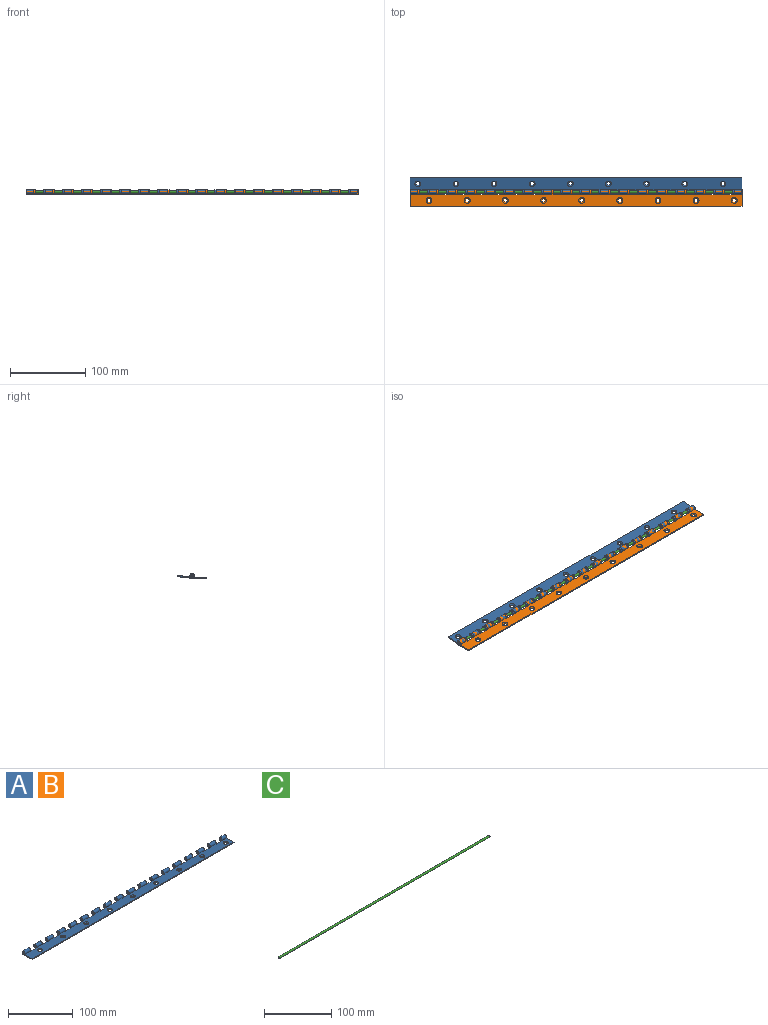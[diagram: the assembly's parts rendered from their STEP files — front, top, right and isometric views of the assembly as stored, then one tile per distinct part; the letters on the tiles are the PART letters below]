
ASSEMBLY  parts=3 mates=2
PART A: 119 faces, bbox 442.2x22.2x6.2 mm
  f0: cylinder r=1.59mm len=12.7mm, axis (-1,0,0), area 105.5mm2, adj f17,f36,f105,f108
  f1: cylinder r=1.59mm len=12.7mm, axis (-1,0,0), area 105.5mm2, adj f17,f37,f102,f106
  f2: cylinder r=1.59mm len=12.7mm, axis (-1,0,0), area 105.5mm2, adj f17,f38,f99,f103
  f3: cylinder r=1.59mm len=12.7mm, axis (-1,0,0), area 105.5mm2, adj f17,f39,f96,f100
  f4: cylinder r=1.59mm len=12.7mm, axis (-1,0,0), area 105.5mm2, adj f17,f40,f93,f97
  f5: cylinder r=1.59mm len=12.7mm, axis (-1,0,0), area 105.5mm2, adj f17,f41,f90,f94
  f6: cylinder r=1.59mm len=12.7mm, axis (-1,0,0), area 105.5mm2, adj f17,f42,f87,f91
  f7: cylinder r=1.59mm len=12.7mm, axis (-1,0,0), area 105.5mm2, adj f17,f43,f84,f88
  f8: cylinder r=1.59mm len=12.7mm, axis (-1,0,0), area 105.5mm2, adj f17,f44,f81,f85
  f9: cylinder r=1.59mm len=12.7mm, axis (-1,0,0), area 105.5mm2, adj f17,f45,f78,f82
  f10: cylinder r=1.59mm len=12.7mm, axis (-1,0,0), area 105.5mm2, adj f17,f46,f75,f79
  f11: cylinder r=1.59mm len=12.7mm, axis (-1,0,0), area 105.5mm2, adj f17,f47,f72,f76
  f12: cylinder r=1.59mm len=12.7mm, axis (-1,0,0), area 105.5mm2, adj f17,f48,f69,f73
  f13: cylinder r=1.59mm len=12.7mm, axis (-1,0,0), area 105.5mm2, adj f17,f49,f66,f70
  f14: cylinder r=1.59mm len=12.7mm, axis (-1,0,0), area 105.5mm2, adj f17,f50,f63,f67
  f15: cylinder r=1.59mm len=12.7mm, axis (-1,0,0), area 105.5mm2, adj f17,f51,f60,f64
  f16: cylinder r=1.59mm len=10.36mm, axis (-1,0,0), area 86mm2, adj f17,f52,f57,f61
  f17: plane 442.16x19.05mm, normal (0,0,1), area 7294.2mm2, adj f0,f1,f2,f3,f4,f5,f6,f7
  f18: plane 442.16x19.05mm, normal (0,0,-1), area 7536.7mm2, adj f19,f20,f21,f22,f23,f24,f25,f26
  f19: cylinder r=3.11mm len=12.7mm, axis (-1,0,0), area 206.7mm2, adj f18,f36,f105,f108
  f20: cylinder r=3.11mm len=12.7mm, axis (-1,0,0), area 206.7mm2, adj f18,f37,f102,f106
  f21: cylinder r=3.11mm len=12.7mm, axis (-1,0,0), area 206.7mm2, adj f18,f38,f99,f103
  f22: cylinder r=3.11mm len=12.7mm, axis (-1,0,0), area 206.7mm2, adj f18,f39,f96,f100
  f23: cylinder r=3.11mm len=12.7mm, axis (-1,0,0), area 206.7mm2, adj f18,f40,f93,f97
  f24: cylinder r=3.11mm len=12.7mm, axis (-1,0,0), area 206.7mm2, adj f18,f41,f90,f94
  f25: cylinder r=3.11mm len=12.7mm, axis (-1,0,0), area 206.7mm2, adj f18,f42,f87,f91
  f26: cylinder r=3.11mm len=12.7mm, axis (-1,0,0), area 206.7mm2, adj f18,f43,f84,f88
  f27: cylinder r=3.11mm len=12.7mm, axis (-1,0,0), area 206.7mm2, adj f18,f44,f81,f85
  f28: cylinder r=3.11mm len=12.7mm, axis (-1,0,0), area 206.7mm2, adj f18,f45,f78,f82
  f29: cylinder r=3.11mm len=12.7mm, axis (-1,0,0), area 206.7mm2, adj f18,f46,f75,f79
  f30: cylinder r=3.11mm len=12.7mm, axis (-1,0,0), area 206.7mm2, adj f18,f47,f72,f76
  f31: cylinder r=3.11mm len=12.7mm, axis (-1,0,0), area 206.7mm2, adj f18,f48,f69,f73
  f32: cylinder r=3.11mm len=12.7mm, axis (-1,0,0), area 206.7mm2, adj f18,f49,f66,f70
  f33: cylinder r=3.11mm len=12.7mm, axis (-1,0,0), area 206.7mm2, adj f18,f50,f63,f67
  f34: cylinder r=3.11mm len=12.7mm, axis (-1,0,0), area 206.7mm2, adj f18,f51,f60,f64
  f35: cylinder r=3.11mm len=10.36mm, axis (-1,0,0), area 168.7mm2, adj f18,f52,f57,f61
  f36: plane 12.7x1.32mm, normal (0,0.5,-0.87), area 19.4mm2, adj f0,f19,f105,f108
  f37: plane 12.7x1.32mm, normal (0,0.5,-0.87), area 19.4mm2, adj f1,f20,f102,f106
  f38: plane 12.7x1.32mm, normal (0,0.5,-0.87), area 19.4mm2, adj f2,f21,f99,f103
  f39: plane 12.7x1.32mm, normal (0,0.5,-0.87), area 19.4mm2, adj f3,f22,f96,f100
  f40: plane 12.7x1.32mm, normal (0,0.5,-0.87), area 19.4mm2, adj f4,f23,f93,f97
  f41: plane 12.7x1.32mm, normal (0,0.5,-0.87), area 19.4mm2, adj f5,f24,f90,f94
  f42: plane 12.7x1.32mm, normal (0,0.5,-0.87), area 19.4mm2, adj f6,f25,f87,f91
  f43: plane 12.7x1.32mm, normal (0,0.5,-0.87), area 19.4mm2, adj f7,f26,f84,f88
  f44: plane 12.7x1.32mm, normal (0,0.5,-0.87), area 19.4mm2, adj f8,f27,f81,f85
  f45: plane 12.7x1.32mm, normal (0,0.5,-0.87), area 19.4mm2, adj f9,f28,f78,f82
  f46: plane 12.7x1.32mm, normal (0,0.5,-0.87), area 19.4mm2, adj f10,f29,f75,f79
  f47: plane 12.7x1.32mm, normal (0,0.5,-0.87), area 19.4mm2, adj f11,f30,f72,f76
  f48: plane 12.7x1.32mm, normal (0,0.5,-0.87), area 19.4mm2, adj f12,f31,f69,f73
  f49: plane 12.7x1.32mm, normal (0,0.5,-0.87), area 19.4mm2, adj f13,f32,f66,f70
  f50: plane 12.7x1.32mm, normal (0,0.5,-0.87), area 19.4mm2, adj f14,f33,f63,f67
  f51: plane 12.7x1.32mm, normal (0,0.5,-0.87), area 19.4mm2, adj f15,f34,f60,f64
  f52: plane 10.36x1.32mm, normal (0,0.5,-0.87), area 15.8mm2, adj f16,f35,f57,f61
  f53: cylinder r=1.59mm len=12.7mm, axis (-1,0,0), area 105.5mm2, adj f17,f56,f58,f109
  f54: plane 442.16x1.52mm, normal (0,-1,0), area 673.9mm2, adj f17,f18,f57,f58
  f55: cylinder r=3.11mm len=12.7mm, axis (-1,0,0), area 206.7mm2, adj f18,f56,f58,f109
  f56: plane 12.7x1.32mm, normal (0,0.5,-0.87), area 19.4mm2, adj f53,f55,f58,f109
  f57: plane 22.16x6.22mm, normal (1,0,0), area 47.8mm2, adj f16,f17,f18,f35,f52,f54
  f58: plane 22.16x6.22mm, normal (-1,0,0), area 47.8mm2, adj f17,f18,f53,f54,f55,f56
  f59: plane 12.7x1.52mm, normal (0,1,0), area 19.4mm2, adj f17,f18,f60,f61
  f60: plane 6.35x6.22mm, normal (1,0,0), area 23.7mm2, adj f15,f17,f18,f34,f51,f59
  f61: plane 6.35x6.22mm, normal (-1,0,0), area 23.7mm2, adj f16,f17,f18,f35,f52,f59
  f62: plane 12.7x1.52mm, normal (0,1,0), area 19.4mm2, adj f17,f18,f63,f64
  f63: plane 6.35x6.22mm, normal (1,0,0), area 23.7mm2, adj f14,f17,f18,f33,f50,f62
  f64: plane 6.35x6.22mm, normal (-1,0,0), area 23.7mm2, adj f15,f17,f18,f34,f51,f62
  f65: plane 12.7x1.52mm, normal (0,1,0), area 19.4mm2, adj f17,f18,f66,f67
  f66: plane 6.35x6.22mm, normal (1,0,0), area 23.7mm2, adj f13,f17,f18,f32,f49,f65
  f67: plane 6.35x6.22mm, normal (-1,0,0), area 23.7mm2, adj f14,f17,f18,f33,f50,f65
  f68: plane 12.7x1.52mm, normal (0,1,0), area 19.4mm2, adj f17,f18,f69,f70
  f69: plane 6.35x6.22mm, normal (1,0,0), area 23.7mm2, adj f12,f17,f18,f31,f48,f68
  f70: plane 6.35x6.22mm, normal (-1,0,0), area 23.7mm2, adj f13,f17,f18,f32,f49,f68
  f71: plane 12.7x1.52mm, normal (0,1,0), area 19.4mm2, adj f17,f18,f72,f73
  f72: plane 6.35x6.22mm, normal (1,0,0), area 23.7mm2, adj f11,f17,f18,f30,f47,f71
  f73: plane 6.35x6.22mm, normal (-1,0,0), area 23.7mm2, adj f12,f17,f18,f31,f48,f71
  f74: plane 12.7x1.52mm, normal (0,1,0), area 19.4mm2, adj f17,f18,f75,f76
  f75: plane 6.35x6.22mm, normal (1,0,0), area 23.7mm2, adj f10,f17,f18,f29,f46,f74
  f76: plane 6.35x6.22mm, normal (-1,0,0), area 23.7mm2, adj f11,f17,f18,f30,f47,f74
  f77: plane 12.7x1.52mm, normal (0,1,0), area 19.4mm2, adj f17,f18,f78,f79
  f78: plane 6.35x6.22mm, normal (1,0,0), area 23.7mm2, adj f9,f17,f18,f28,f45,f77
  f79: plane 6.35x6.22mm, normal (-1,0,0), area 23.7mm2, adj f10,f17,f18,f29,f46,f77
  f80: plane 12.7x1.52mm, normal (0,1,0), area 19.4mm2, adj f17,f18,f81,f82
  f81: plane 6.35x6.22mm, normal (1,0,0), area 23.7mm2, adj f8,f17,f18,f27,f44,f80
  f82: plane 6.35x6.22mm, normal (-1,0,0), area 23.7mm2, adj f9,f17,f18,f28,f45,f80
  f83: plane 12.7x1.52mm, normal (0,1,0), area 19.4mm2, adj f17,f18,f84,f85
  f84: plane 6.35x6.22mm, normal (1,0,0), area 23.7mm2, adj f7,f17,f18,f26,f43,f83
  f85: plane 6.35x6.22mm, normal (-1,0,0), area 23.7mm2, adj f8,f17,f18,f27,f44,f83
  f86: plane 12.7x1.52mm, normal (0,1,0), area 19.4mm2, adj f17,f18,f87,f88
  f87: plane 6.35x6.22mm, normal (1,0,0), area 23.7mm2, adj f6,f17,f18,f25,f42,f86
  f88: plane 6.35x6.22mm, normal (-1,0,0), area 23.7mm2, adj f7,f17,f18,f26,f43,f86
  f89: plane 12.7x1.52mm, normal (0,1,0), area 19.4mm2, adj f17,f18,f90,f91
  f90: plane 6.35x6.22mm, normal (1,0,0), area 23.7mm2, adj f5,f17,f18,f24,f41,f89
  f91: plane 6.35x6.22mm, normal (-1,0,0), area 23.7mm2, adj f6,f17,f18,f25,f42,f89
  f92: plane 12.7x1.52mm, normal (0,1,0), area 19.4mm2, adj f17,f18,f93,f94
  f93: plane 6.35x6.22mm, normal (1,0,0), area 23.7mm2, adj f4,f17,f18,f23,f40,f92
  f94: plane 6.35x6.22mm, normal (-1,0,0), area 23.7mm2, adj f5,f17,f18,f24,f41,f92
  f95: plane 12.7x1.52mm, normal (0,1,0), area 19.4mm2, adj f17,f18,f96,f97
  f96: plane 6.35x6.22mm, normal (1,0,0), area 23.7mm2, adj f3,f17,f18,f22,f39,f95
  f97: plane 6.35x6.22mm, normal (-1,0,0), area 23.7mm2, adj f4,f17,f18,f23,f40,f95
  f98: plane 12.7x1.52mm, normal (0,1,0), area 19.4mm2, adj f17,f18,f99,f100
  f99: plane 6.35x6.22mm, normal (1,0,0), area 23.7mm2, adj f2,f17,f18,f21,f38,f98
  f100: plane 6.35x6.22mm, normal (-1,0,0), area 23.7mm2, adj f3,f17,f18,f22,f39,f98
  f101: plane 12.7x1.52mm, normal (0,1,0), area 19.4mm2, adj f17,f18,f102,f103
  f102: plane 6.35x6.22mm, normal (1,0,0), area 23.7mm2, adj f1,f17,f18,f20,f37,f101
  f103: plane 6.35x6.22mm, normal (-1,0,0), area 23.7mm2, adj f2,f17,f18,f21,f38,f101
  f104: plane 12.7x1.52mm, normal (0,1,0), area 19.4mm2, adj f17,f18,f105,f106
  f105: plane 6.35x6.22mm, normal (1,0,0), area 23.7mm2, adj f0,f17,f18,f19,f36,f104
  f106: plane 6.35x6.22mm, normal (-1,0,0), area 23.7mm2, adj f1,f17,f18,f20,f37,f104
  f107: plane 12.7x1.52mm, normal (0,1,0), area 19.4mm2, adj f17,f18,f108,f109
  f108: plane 6.35x6.22mm, normal (-1,0,0), area 23.7mm2, adj f0,f17,f18,f19,f36,f107
  f109: plane 6.35x6.22mm, normal (1,0,0), area 23.7mm2, adj f17,f18,f53,f55,f56,f107
  f110: cone r=1.83mm half-angle=41deg, axis (0,0,1), area 41.1mm2, adj f17,f18
  f111: cone r=1.83mm half-angle=41deg, axis (0,0,1), area 41.1mm2, adj f17,f18
  f112: cone r=1.83mm half-angle=41deg, axis (0,0,1), area 41.1mm2, adj f17,f18
  f113: cone r=1.83mm half-angle=41deg, axis (0,0,1), area 41.1mm2, adj f17,f18
  f114: cone r=1.83mm half-angle=41deg, axis (0,0,1), area 41.1mm2, adj f17,f18
  f115: cone r=1.83mm half-angle=41deg, axis (0,0,1), area 41.1mm2, adj f17,f18
  f116: cone r=1.83mm half-angle=41deg, axis (0,0,1), area 41.1mm2, adj f17,f18
  f117: cone r=1.83mm half-angle=41deg, axis (0,0,1), area 41.1mm2, adj f17,f18
  f118: cone r=1.83mm half-angle=41deg, axis (0,0,1), area 41.1mm2, adj f17,f18
PART B: same geometry as A
PART C: 3 faces, bbox 442.2x3.2x3.2 mm
  f0: plane 3.18x3.18mm, normal (1,0,0), area 7.9mm2, adj f1
  f1: cylinder r=1.59mm len=442.16mm, axis (-1,0,0), area 4410.4mm2, adj f0,f2
  f2: plane 3.18x3.18mm, normal (-1,0,0), area 7.9mm2, adj f1
PLACE A rot(axis=(0,-0.06,1),180deg) t=(442.16,0,0)mm
PLACE B at identity
PLACE C at identity
MATE revolute B.f0 <-> C.f1  axis (-1,0,0) through (0,0,0)mm
MATE revolute A.f0 <-> C.f1  axis (1,0,0) through (442.16,0,0)mm
